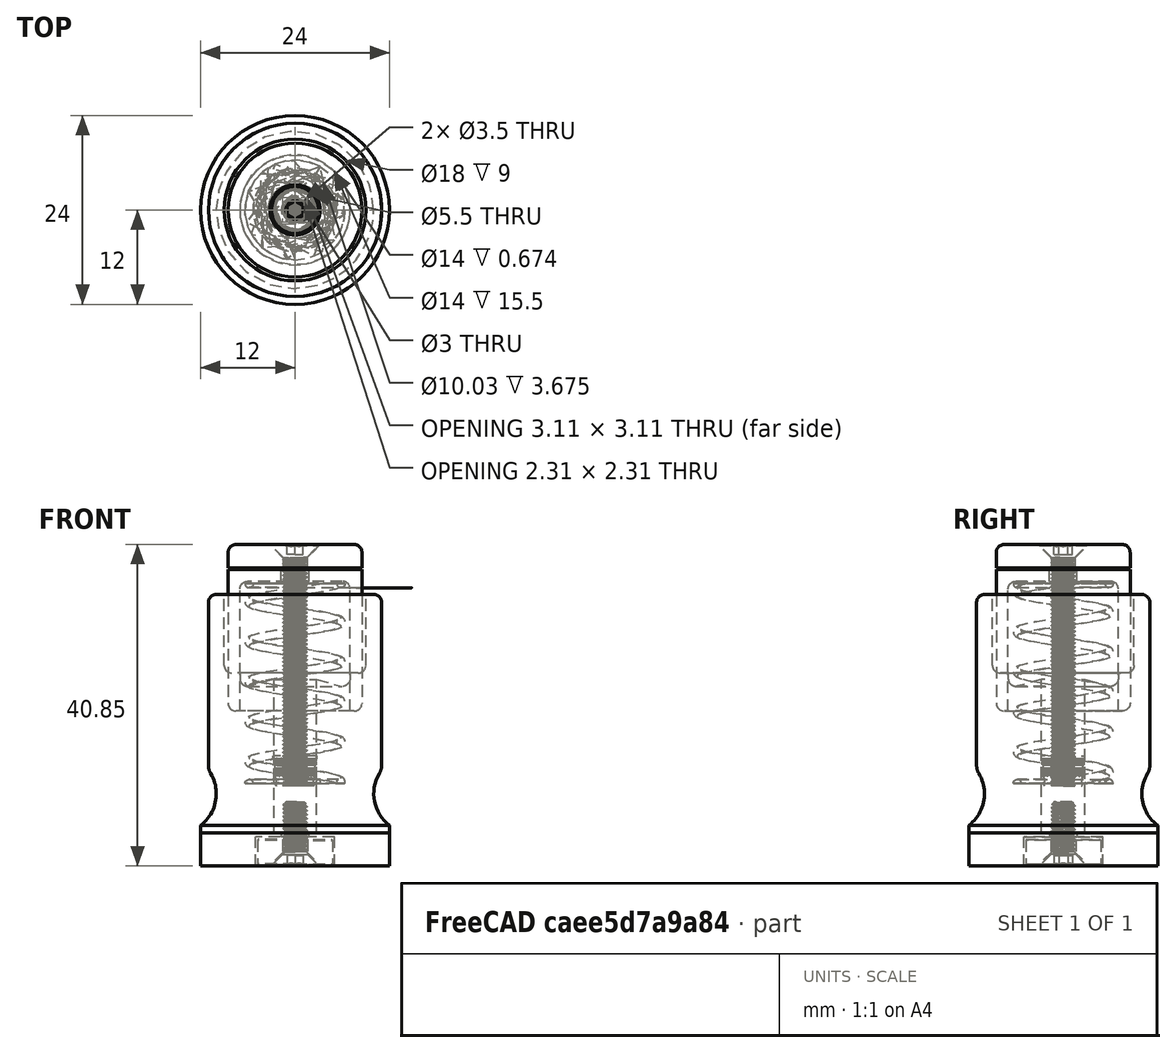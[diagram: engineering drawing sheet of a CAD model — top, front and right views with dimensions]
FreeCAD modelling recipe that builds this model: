
FCSTD DOCUMENT  (FreeCAD 1.0R39109 (Git))
Label: mag-clamp
License: All rights reserved
LicenseURL: https://en.wikipedia.org/wiki/All_rights_reserved
objects: App::FeaturePython×11, App::Link×10, Sketcher::SketchObject×9, Part::Feature×5, PartDesign::Fillet×5, PartDesign::Revolution×4, PartDesign::Body×4, PartDesign::Pocket×2, PartDesign::Groove×1, App::VarSet×1, App::Part×1, Assembly::JointGroup×1, Assembly::AssemblyObject×1, Measure::MeasureDistance×1, App::DocumentObjectGroup×1
note: 63 computed .brp shape members not serialized (recipe doc carries the construction recipe); baked Part::Feature solids carry a one-line shape summary decoded from their .brp

FEATURE [Sketcher::SketchObject] Sketch
  ArcFitTolerance = 1e-06
  AttachmentSupport = -> [XZ_Plane]
  FullyConstrained = true
  MakeInternals = false
  MapMode = 5
  Placement = pos=(0,0,0) rot=(1,0,0;1.5708rad)
  expr: Constraints[22] = VarSet.height
  sketch-geometry (14):
    g0: LineSegment StartX=0 StartY=0 StartZ=0 EndX=12 EndY=0 EndZ=0
    g1: LineSegment StartX=7 StartY=20.325 StartZ=0 EndX=7 EndY=18.325 EndZ=0
    g2: LineSegment StartX=9 StartY=30.325 StartZ=0 EndX=11 EndY=30.325 EndZ=0
    g3: LineSegment [constr] StartX=7 StartY=18.325 StartZ=0 EndX=5 EndY=18.325 EndZ=0
    g4: LineSegment [constr] StartX=5 StartY=18.325 StartZ=0 EndX=5 EndY=20.325 EndZ=0
    g5: LineSegment [constr] StartX=5 StartY=20.325 StartZ=0 EndX=0 EndY=20.325 EndZ=0
    g6: LineSegment StartX=0 StartY=0 StartZ=0 EndX=0 EndY=20.325 EndZ=0
    g7: LineSegment StartX=7 StartY=20.325 StartZ=0 EndX=9 EndY=20.325 EndZ=0
    g8: LineSegment StartX=9 StartY=20.325 StartZ=0 EndX=9 EndY=30.325 EndZ=0
    g9: LineSegment [constr] StartX=5 StartY=20.325 StartZ=0 EndX=7 EndY=20.325 EndZ=0
    g10: LineSegment StartX=11 StartY=30.325 StartZ=0 EndX=11 EndY=8 EndZ=0
    g11: LineSegment StartX=12 StartY=0 StartZ=0 EndX=12 EndY=1 EndZ=0
    g12: ArcOfCircle CenterX=15 CenterY=5 CenterZ=0 NormalX=0 NormalY=0 NormalZ=1 AngleXU=0 Radius=5 StartAngle=2.49809 EndAngle=4.06889
    g13: LineSegment StartX=0 StartY=20.325 StartZ=0 EndX=7 EndY=18.325 EndZ=0
  constraints (40):
    c: Coincident(g-1,g0)
    c: PointOnObject(g0,g-1)
    c: Vertical(g1)
    c: Horizontal(g3)
    c: Vertical(g4)
    c: Coincident(g5,g4)
    c: Horizontal(g5)
    c: Coincident(g3,g1)
    c: Horizontal(g2)
    c: Coincident(g3,g4)
    c: DistanceX(g6,g3) = 5
    c: Coincident(g6,g0)
    c: DistanceX(g0,g1) = 7
    c: DistanceX(g0,g0) = 12
    c: DistanceY(g4,g4) = 2
    c: Coincident(g6,g5)
    c: PointOnObject(g5,g-2)
    c: Horizontal(g7)
    c: Coincident(g7,g8)
    c: Vertical(g8)
    c: Coincident(g1,g7)
    c: Coincident(g2,g8)
    c: DistanceY(g0,g2) = 30.325
    c: DistanceY(g8,g8) = 10
    c: DistanceX(g7,g7) = 2
    c: DistanceX(g2,g2) = 2
    c: Coincident(g9,g4)
    c: Coincident(g9,g1)
    c: Horizontal(g9)
    c: Coincident(g10,g2)
    c: Vertical(g10)
    c: Coincident(g11,g0)
    c: Coincident(g12,g11)
    c: Coincident(g12,g10)
    c: Vertical(g11)
    c: DistanceY(g11,g11) = 1
    c: Radius(g12) = 5
    c: DistanceY(g0,g10) = 8
    c: Coincident(g13,g5)
    c: Coincident(g13,g1)
FEATURE [PartDesign::Revolution] Revolution
  Angle = 360
  Angle2 = 60
  Axis = (0,2e-16,1)
  Base = (0,0,0)
  Placement = pos=(0,0,0) rot=(1,0,0;1.5708rad)
  Profile = -> Sketch
  ReferenceAxis = -> Sketch [V_Axis]
  Refine = true
  Reversed = true
  Suppressed = false
  Type = 0
FEATURE [Part::Feature] Part__Feature  label="9657K312_Compression Spring"
  Placement = pos=(0,0,19) rot=(0,0,1;0rad)
  shape: bbox 14.01 x 14.01 x 26.49 mm, 6 faces (baked)
FEATURE [Part::Feature] Part__Feature001  label="5862K919_Neodymium Magnet"
  Placement = pos=(0,-5e-16,-2.4) rot=(1,0,0;4.71239rad)
  shape: bbox 9.525 x 9.525 x 3.175 mm, 12 faces (baked)
FEATURE [Sketcher::SketchObject] Sketch002
  ArcFitTolerance = 1e-06
  AttachmentSupport = -> [XZ_Plane001]
  FullyConstrained = true
  MakeInternals = false
  MapMode = 5
  Placement = pos=(0,0,0) rot=(1,0,0;1.5708rad)
  expr: Constraints[14] = VarSet.retainer_height
  sketch-geometry (6):
    g0: LineSegment StartX=1.75 StartY=33.5 StartZ=0 EndX=8.5 EndY=33.5 EndZ=0
    g1: LineSegment StartX=8.5 StartY=33.5 StartZ=0 EndX=8.5 EndY=15.5 EndZ=0
    g2: LineSegment StartX=8.5 StartY=15.5 StartZ=0 EndX=7 EndY=15.5 EndZ=0
    g3: LineSegment StartX=7 StartY=15.5 StartZ=0 EndX=7 EndY=32 EndZ=0
    g4: LineSegment StartX=7 StartY=32 StartZ=0 EndX=1.75 EndY=32 EndZ=0
    g5: LineSegment StartX=1.75 StartY=32 StartZ=0 EndX=1.75 EndY=33.5 EndZ=0
  constraints (18):
    c: Horizontal(g0)
    c: Coincident(g0,g1)
    c: Vertical(g1)
    c: Coincident(g1,g2)
    c: Horizontal(g2)
    c: Coincident(g2,g3)
    c: Vertical(g3)
    c: Coincident(g3,g4)
    c: Horizontal(g4)
    c: Coincident(g4,g5)
    c: Vertical(g5)
    c: Coincident(g0,g5)
    c: DistanceX(g2,g2) = 1.5
    c: DistanceY(g5,g5) = 1.5
    c: DistanceY(g1,g1) = 18
    c: DistanceX(g-1,g0) = 1.75
    c: DistanceX(g-1,g3) = 7
    c: DistanceY(g-1,g4) = 32
FEATURE [PartDesign::Revolution] Revolution001
  Angle = 360
  Angle2 = 60
  Axis = (0,2e-16,1)
  Base = (0,0,0)
  Placement = pos=(0,0,0) rot=(1,0,0;1.5708rad)
  Profile = -> Sketch002
  ReferenceAxis = -> Sketch002 [V_Axis]
  Refine = true
  Reversed = true
  Suppressed = false
  Type = 0
FEATURE [Sketcher::SketchObject] Sketch003
  ArcFitTolerance = 1e-06
  AttachmentSupport = -> [XZ_Plane002]
  FullyConstrained = false
  MakeInternals = false
  MapMode = 5
  Placement = pos=(0,0,0) rot=(1,0,0;1.5708rad)
  sketch-geometry (4):
    g0: LineSegment StartX=0 StartY=36.6662 StartZ=0 EndX=0 EndY=33.6662 EndZ=0
    g1: LineSegment StartX=0 StartY=33.6662 StartZ=0 EndX=8.5 EndY=33.6662 EndZ=0
    g2: LineSegment StartX=8.5 StartY=33.6662 StartZ=0 EndX=8.5 EndY=36.6662 EndZ=0
    g3: LineSegment StartX=8.5 StartY=36.6662 StartZ=0 EndX=0 EndY=36.6662 EndZ=0
  constraints (11):
    c: Coincident(g0,g1)
    c: Coincident(g1,g2)
    c: Coincident(g2,g3)
    c: Coincident(g3,g0)
    c: Vertical(g0)
    c: Vertical(g2)
    c: Horizontal(g1)
    c: Horizontal(g3)
    c: PointOnObject(g0,g-2)
    c: DistanceX(g3,g3) = 8.5
    c: Distance(g2,g2) = 3
FEATURE [PartDesign::Revolution] Revolution002
  Angle = 360
  Angle2 = 60
  Axis = (0,2e-16,1)
  Base = (0,0,0)
  Placement = pos=(0,0,0) rot=(1,0,0;1.5708rad)
  Profile = -> Sketch003
  ReferenceAxis = -> Sketch003 [V_Axis]
  Refine = true
  Reversed = true
  Suppressed = false
  Type = 0
FEATURE [PartDesign::Fillet] Fillet
  Base = -> Revolution002 [Edge2]
  BaseFeature = -> Revolution002
  Placement = pos=(0,0,0) rot=(1,0,0;1.5708rad)
  Radius = 1
  Refine = true
  SupportTransform = false
  Suppressed = false
  UseAllEdges = false
FEATURE [Sketcher::SketchObject] Sketch004
  ArcFitTolerance = 1e-06
  AttachmentSupport = -> [XZ_Plane002]
  ExternalGeometry = -> [Fillet]
  FullyConstrained = false
  MakeInternals = false
  MapMode = 5
  Placement = pos=(0,0,0) rot=(1,0,0;1.5708rad)
  sketch-geometry (5):
    g0: LineSegment StartX=0 StartY=36.6662 StartZ=0 EndX=0 EndY=29.3467 EndZ=0
    g1: LineSegment StartX=0 StartY=29.3467 StartZ=0 EndX=1.5 EndY=29.3467 EndZ=0
    g2: LineSegment StartX=0 StartY=36.6662 StartZ=0 EndX=3.2 EndY=36.6662 EndZ=0
    g3: LineSegment StartX=3.2 StartY=36.6662 StartZ=0 EndX=1.5 EndY=34.9662 EndZ=0
    g4: LineSegment StartX=1.5 StartY=34.9662 StartZ=0 EndX=1.5 EndY=29.3467 EndZ=0
  constraints (14):
    c: PointOnObject(g0,g-2)
    c: Vertical(g0)
    c: Coincident(g1,g0)
    c: Horizontal(g1)
    c: Coincident(g2,g0)
    c: Horizontal(g2)
    c: Coincident(g3,g2)
    c: Coincident(g4,g3)
    c: Coincident(g4,g1)
    c: Vertical(g4)
    c: DistanceX(g1,g1) = 1.5
    c: Angle(g3,g-2) = 0.785398
    c: PointOnObject(g2,g-3)
    c: DistanceY(g3,g-3) = 1.7
FEATURE [PartDesign::Groove] Groove
  Angle = 360
  Angle2 = 60
  Axis = (0,2e-16,1)
  Base = (0,0,0)
  BaseFeature = -> Fillet
  Placement = pos=(0,0,0) rot=(1,0,0;1.5708rad)
  Profile = -> Sketch004
  ReferenceAxis = -> Sketch004 [V_Axis]
  Refine = true
  Suppressed = false
  Type = 0
FEATURE [PartDesign::Body] Body002  label="Cap"
  AllowCompound = false
  Group = -> [Sketch003,Revolution002,Fillet,Sketch004,Groove]
  Origin = -> Origin002
  Tip = -> Groove
FEATURE [Sketcher::SketchObject] Sketch005
  ArcFitTolerance = 1e-06
  AttachmentSupport = -> [XZ_Plane003]
  FullyConstrained = true
  MakeInternals = false
  MapMode = 5
  Placement = pos=(0,0,0) rot=(1,0,0;1.5708rad)
  expr: Constraints[14] = VarSet.bottom_thk
  expr: Constraints[15] = VarSet.magnet_od / 2 + 0.25 mm
  sketch-geometry (6):
    g0: LineSegment StartX=0 StartY=0 StartZ=0 EndX=12 EndY=0 EndZ=0
    g1: LineSegment StartX=12 StartY=0 StartZ=0 EndX=12 EndY=-4.175 EndZ=0
    g2: LineSegment StartX=12 StartY=-4.175 StartZ=0 EndX=5.0125 EndY=-4.175 EndZ=0
    g3: LineSegment StartX=5.0125 StartY=-4.175 StartZ=0 EndX=5.0125 EndY=-0.5 EndZ=0
    g4: LineSegment StartX=5.0125 StartY=-0.5 StartZ=0 EndX=0 EndY=-0.5 EndZ=0
    g5: LineSegment StartX=0 StartY=-0.5 StartZ=0 EndX=0 EndY=0 EndZ=0
  constraints (17):
    c: Coincident(g-1,g0)
    c: PointOnObject(g0,g-1)
    c: Coincident(g0,g1)
    c: Vertical(g1)
    c: Coincident(g1,g2)
    c: Horizontal(g2)
    c: Coincident(g2,g3)
    c: Vertical(g3)
    c: Coincident(g3,g4)
    c: PointOnObject(g4,g-2)
    c: Horizontal(g4)
    c: Coincident(g4,g5)
    c: Coincident(g5,g0)
    c: DistanceX(g0,g0) = 12
    c: DistanceY(g1,g1) = 4.175
    c: DistanceX(g4,g4) = 5.0125
    c: DistanceY(g5,g5) = 0.5
FEATURE [PartDesign::Revolution] Revolution003
  Angle = 360
  Angle2 = 60
  Axis = (0,2e-16,1)
  Base = (0,0,0)
  Placement = pos=(0,0,0) rot=(1,0,0;1.5708rad)
  Profile = -> Sketch005
  ReferenceAxis = -> Sketch005 [V_Axis]
  Refine = true
  Reversed = true
  Suppressed = false
  Type = 0
FEATURE [Sketcher::SketchObject] Sketch006
  ArcFitTolerance = 1e-06
  AttachmentSupport = -> [Revolution003]
  FullyConstrained = true
  MakeInternals = false
  MapMode = 5
  Placement = pos=(0,-1e-16,-0.5) rot=(1,0,0;3.14159rad)
  sketch-geometry (1):
    g0: Circle CenterX=0 CenterY=0 CenterZ=0 NormalX=0 NormalY=0 NormalZ=1 AngleXU=0 Radius=1.75
  constraints (2):
    c: Coincident(g0,g-1)
    c: Diameter(g0) = 3.5
FEATURE [PartDesign::Pocket] Pocket001
  BaseFeature = -> Revolution003
  Direction = (0,0,1)
  Length = 5
  Length2 = 5
  Placement = pos=(0,0,0) rot=(1,0,0;1.5708rad)
  Profile = -> Sketch006
  ReferenceAxis = -> Sketch006 [N_Axis]
  Refine = true
  Suppressed = false
  Type = 1
FEATURE [PartDesign::Body] Body003  label="Magnet"
  AllowCompound = false
  Group = -> [Sketch005,Revolution003,Sketch006,Pocket001]
  Origin = -> Origin003
  Tip = -> Pocket001
FEATURE [Part::Feature] Part__Feature002  label="94180A331_Tapered Heat-Set Inserts for Plastic"
  Placement = pos=(0,0,7.9) rot=(0,0,1;0rad)
  shape: bbox 5.56 x 5.56 x 4.684 mm, 233 faces (baked)
FEATURE [Part::Feature] Part__Feature004  label="92125A128_18-8 Stainless Steel Hex Drive Flat Head Screw"
  Placement = pos=(0,0,0) rot=(0,1,0;3.14159rad)
  shape: bbox 6.001 x 6.001 x 8.204 mm, 52 faces (baked)
FEATURE [Part::Feature] Part__Feature005  label="92125A140_18-8 Stainless Steel Hex Drive Flat Head Screw"
  Placement = pos=(0,0,21.6) rot=(0,0,1;0rad)
  shape: bbox 6.001 x 6.001 x 30.2 mm, 140 faces (baked)
FEATURE [App::VarSet] VarSet
  bottom_thk = 4.175
  heatset_od = 5.5
  height = 30.325
  magnet_od = 9.525
  magnet_thk = 3.175
  retainer_height = 18
  total_height = 50
  expr: bottom_thk = magnet_thk + 1 mm
  expr: height = total_height - bottom_thk - retainer_height + 2.5 mm
FEATURE [PartDesign::Fillet] Fillet001
  Base = -> Revolution [Edge6,Edge12,Edge9]
  BaseFeature = -> Revolution
  Placement = pos=(0,0,0) rot=(1,0,0;1.5708rad)
  Radius = 1
  Refine = true
  SupportTransform = false
  Suppressed = false
  UseAllEdges = false
FEATURE [App::Link] Base  label="Base001"
  LinkedObject = -> Body
FEATURE [App::FeaturePython] GroundedJoint  # Assembly grounded joint (typed FeaturePython)
  ObjectToGround = -> Base
FEATURE [App::Link] Cap  label="Cap001"
  LinkPlacement = pos=(-3.38e-14,3.17e-14,11.7731) rot=(0,0,1;4.71239rad)
  LinkedObject = -> Body002
  Placement = pos=(-3.38e-14,3.17e-14,11.7731) rot=(0,0,1;4.71239rad)
FEATURE [App::Link] Magnet  label="Magnet001"
  LinkedObject = -> Body003
FEATURE [App::Link] _2125A140_18_8_Stainless_Steel_Hex_Drive_Flat_Head_Screw  label="92125A140_18-8 Stainless Steel Hex Drive Flat Head Screw001"
  LinkPlacement = pos=(-1.11e-14,1.43e-14,33.3243) rot=(0,0,1;0rad)
  LinkedObject = -> Part__Feature005
  Placement = pos=(-1.11e-14,1.43e-14,33.3243) rot=(0,0,1;0rad)
FEATURE [App::Link] _4180A331_Tapered_Heat_Set_Inserts_for_Plastic  label="94180A331_Tapered Heat-Set Inserts for Plastic002"
  LinkPlacement = pos=(0,0,1.9) rot=(1,0,0;3.14159rad)
  LinkedObject = -> Part__Feature002
  Placement = pos=(0,0,1.9) rot=(1,0,0;3.14159rad)
FEATURE [App::Link] _4180A331_Tapered_Heat_Set_Inserts_for_Plastic001  label="94180A331_Tapered Heat-Set Inserts for Plastic003"
  LinkPlacement = pos=(0,4.5e-15,17.6393) rot=(0,0,1;4.71239rad)
  LinkedObject = -> Part__Feature002
  Placement = pos=(0,4.5e-15,17.6393) rot=(0,0,1;4.71239rad)
FEATURE [App::Link] _2125A128_18_8_Stainless_Steel_Hex_Drive_Flat_Head_Screw  label="92125A128_18-8 Stainless Steel Hex Drive Flat Head Screw001"
  LinkPlacement = pos=(-5.3e-15,3.2e-15,0.0975) rot=(1,0,0;3.14159rad)
  LinkedObject = -> Part__Feature004
  Placement = pos=(-5.3e-15,3.2e-15,0.0975) rot=(1,0,0;3.14159rad)
FEATURE [App::Link] _862K919_Neodymium_Magnet  label="5862K919_Neodymium Magnet001"
  LinkPlacement = pos=(-5.6e-15,3.5e-15,-2.0875) rot=(-0.57735,0.57735,-0.57735;2.0944rad)
  LinkedObject = -> Part__Feature001
  Placement = pos=(-5.6e-15,3.5e-15,-2.0875) rot=(-0.57735,0.57735,-0.57735;2.0944rad)
FEATURE [Sketcher::SketchObject] Sketch008
  ArcFitTolerance = 1e-06
  AttachmentSupport = -> [Part__Feature]
  FullyConstrained = false
  MakeInternals = false
  MapMode = 5
  Placement = pos=(0,0,6.3) rot=(1,0,0;3.14159rad)
  sketch-geometry (1):
    g0: Circle CenterX=0 CenterY=0 CenterZ=0 NormalX=0 NormalY=0 NormalZ=1 AngleXU=0 Radius=4.4961
  constraints (1):
    c: Coincident(g0,g-1)
FEATURE [App::Link] Spring  label="Spring001"
  LinkPlacement = pos=(0,4.5e-15,12.2393) rot=(0,0,1;4.71239rad)
  LinkedObject = -> Part
  Placement = pos=(0,4.5e-15,12.2393) rot=(0,0,1;4.71239rad)
FEATURE [Sketcher::SketchObject] Sketch010
  ArcFitTolerance = 1e-06
  AttachmentSupport = -> [Fillet001]
  FullyConstrained = true
  MakeInternals = false
  MapMode = 5
  Placement = pos=(0,6.7e-15,30.325) rot=(0,0,1;3.14159rad)
  expr: Constraints[1] = VarSet.heatset_od
  sketch-geometry (1):
    g0: Circle CenterX=0 CenterY=0 CenterZ=0 NormalX=0 NormalY=0 NormalZ=1 AngleXU=0 Radius=2.75
  constraints (2):
    c: Coincident(g0,g-1)
    c: Diameter(g0) = 5.5
FEATURE [PartDesign::Pocket] Pocket
  BaseFeature = -> Fillet001
  Direction = (0,0,-1)
  Length = 5
  Length2 = 5
  Placement = pos=(0,0,0) rot=(1,0,0;1.5708rad)
  Profile = -> Sketch010
  ReferenceAxis = -> Sketch010 [N_Axis]
  Refine = true
  Suppressed = false
  Type = 1
FEATURE [PartDesign::Fillet] Fillet002
  Base = -> Pocket [Edge3]
  BaseFeature = -> Pocket
  Placement = pos=(0,0,0) rot=(1,0,0;1.5708rad)
  Radius = 2
  Refine = true
  SupportTransform = false
  Suppressed = false
  UseAllEdges = false
FEATURE [PartDesign::Body] Body  label="Base"
  AllowCompound = false
  Group = -> [Sketch,Revolution,Fillet001,Sketch010,Pocket,Fillet002]
  Origin = -> Origin
  Tip = -> Fillet002
FEATURE [PartDesign::Fillet] Fillet003
  Base = -> Revolution001 [Edge3]
  BaseFeature = -> Revolution001
  Placement = pos=(0,0,0) rot=(1,0,0;1.5708rad)
  Radius = 1
  Refine = true
  SupportTransform = false
  Suppressed = false
  UseAllEdges = false
FEATURE [App::FeaturePython] Joint008  label="Fixed006"  # Assembly joint (typed FeaturePython)
  Activated = true
  AngleMax = 0
  AngleMin = 0
  Detach1 = false
  Detach2 = false
  Distance = 0
  Distance2 = 0
  EnableAngleMax = false
  EnableAngleMin = false
  EnableLengthMax = false
  EnableLengthMin = false
  JointType = 0 (Fixed)
  LengthMax = 0
  LengthMin = 0
  Placement1 = pos=(0,0,1.9) rot=(0,0,1;0rad)
  Reference1 = -> Assembly [_4180A331_Tapered_Heat_Set_Inserts_for_Plastic.Edge61,_4180A331_Tapered_Heat_Set_Inserts_for_Plastic.Edge61]
  Reference2 = -> Assembly [Base.?Edge13,Base.?Edge13]
FEATURE [App::FeaturePython] Joint  label="Fixed"  # Assembly joint (typed FeaturePython)
  Activated = true
  AngleMax = 0
  AngleMin = 0
  Detach1 = false
  Detach2 = false
  Distance = 0
  Distance2 = 0
  EnableAngleMax = false
  EnableAngleMin = false
  EnableLengthMax = false
  EnableLengthMin = false
  JointType = 0 (Fixed)
  LengthMax = 0
  LengthMin = 0
  Placement1 = pos=(0,0,0) rot=(1,0,0;3.14159rad)
  Reference1 = -> Assembly [Magnet.Edge1,Magnet.Edge1]
  Reference2 = -> Assembly [Base.?Edge16,Base.?Edge16]
FEATURE [App::FeaturePython] Joint005  label="Fixed003"  # Assembly joint (typed FeaturePython)
  Activated = true
  AngleMax = 0
  AngleMin = 0
  Detach1 = false
  Detach2 = false
  Distance = 0
  Distance2 = 0
  EnableAngleMax = false
  EnableAngleMin = false
  EnableLengthMax = false
  EnableLengthMin = false
  JointType = 0 (Fixed)
  LengthMax = 0
  LengthMin = 0
  Placement1 = pos=(3.5e-15,-1.5875,5.2e-15) rot=(0.57735,-0.57735,0.57735;2.0944rad)
  Placement2 = pos=(0,-1e-16,-0.5) rot=(1,0,0;3.14159rad)
  Reference1 = -> Assembly [_862K919_Neodymium_Magnet.Edge24,_862K919_Neodymium_Magnet.Edge24]
  Reference2 = -> Assembly [Magnet.Edge8,Magnet.Edge8]
FEATURE [App::FeaturePython] Joint006  label="Fixed004"  # Assembly joint (typed FeaturePython)
  Activated = true
  AngleMax = 0
  AngleMin = 0
  Detach1 = false
  Detach2 = false
  Distance = 0
  Distance2 = 0
  EnableAngleMax = false
  EnableAngleMin = false
  EnableLengthMax = false
  EnableLengthMin = false
  JointType = 0 (Fixed)
  LengthMax = 0
  LengthMin = 0
  Placement1 = pos=(0,-1e-16,0.915) rot=(0,0,-1;1.5708rad)
  Placement2 = pos=(0,-1.27,0) rot=(0,0.707107,0.707107;3.14159rad)
  Reference1 = -> Assembly [_2125A128_18_8_Stainless_Steel_Hex_Drive_Flat_Head_Screw.Face29,_2125A128_18_8_Stainless_Steel_Hex_Drive_Flat_Head_Screw.Face29]
  Reference2 = -> Assembly [_862K919_Neodymium_Magnet.Face3,_862K919_Neodymium_Magnet.Face3]
FEATURE [App::FeaturePython] Joint004  label="Fixed002"  # Assembly joint (typed FeaturePython)
  Activated = true
  AngleMax = 0
  AngleMin = 0
  Detach1 = false
  Detach2 = false
  Distance = 0
  Distance2 = 0
  EnableAngleMax = false
  EnableAngleMin = false
  EnableLengthMax = false
  EnableLengthMin = false
  JointType = 0 (Fixed)
  LengthMax = 0
  LengthMin = 0
  Placement1 = pos=(0,7.4e-15,33.4662) rot=(0,0,1;0rad)
  Placement2 = pos=(0,-1e-16,11.915) rot=(0,0,-1;1.5708rad)
  Reference1 = -> Assembly [Cap.Face6,Cap.Face6]
  Reference2 = -> Assembly [_2125A140_18_8_Stainless_Steel_Hex_Drive_Flat_Head_Screw.Face119,_2125A140_18_8_Stainless_Steel_Hex_Drive_Flat_Head_Screw.Face119]
FEATURE [App::FeaturePython] Joint010  label="Fixed008"  # Assembly joint (typed FeaturePython)
  Activated = true
  AngleMax = 0
  AngleMin = 0
  Detach1 = false
  Detach2 = false
  Distance = 0
  Distance2 = 0
  EnableAngleMax = false
  EnableAngleMin = false
  EnableLengthMax = false
  EnableLengthMin = false
  JointType = 0 (Fixed)
  LengthMax = 0
  LengthMin = 0
  Offset2 = pos=(0,0,-1) rot=(0,0,1;0rad)
  Placement2 = pos=(0,4.5e-15,18.5393) rot=(0,0,-1;1.5708rad)
  Reference1 = -> Assembly [Spring.Sketch008.Edge1,Spring.Sketch008.Edge1]
  Reference2 = -> Assembly [Base.Edge19,Base.Edge19]
FEATURE [App::FeaturePython] Joint002  label="Cylindrical"  # Assembly joint (typed FeaturePython)
  Activated = true
  AngleMax = 0
  AngleMin = 0
  Detach1 = false
  Detach2 = false
  Distance = 0
  Distance2 = 0
  EnableAngleMax = false
  EnableAngleMin = false
  EnableLengthMax = false
  EnableLengthMin = false
  JointType = 2 (Cylindrical)
  LengthMax = 0
  LengthMin = 0
  Placement1 = pos=(6.1e-14,6.27e-14,-36.9393) rot=(0,0,-1;4.71239rad)
  Reference1 = -> Assembly [Retainer.?Face2,Retainer.?Face2]
  Reference2 = -> Assembly [Base.?Face6,Base.Edge25]
FEATURE [App::FeaturePython] Joint003  label="Fixed001"  # Assembly joint (typed FeaturePython)
  Activated = true
  AngleMax = 0
  AngleMin = 0
  Detach1 = false
  Detach2 = false
  Distance = 0
  Distance2 = 0
  EnableAngleMax = false
  EnableAngleMin = false
  EnableLengthMax = false
  EnableLengthMin = false
  JointType = 0 (Fixed)
  LengthMax = 0
  LengthMin = 0
  Placement1 = pos=(0,7.5e-15,33.6662) rot=(1,0,0;3.14159rad)
  Placement2 = pos=(0,7.4e-15,33.5) rot=(1,0,0;3.14159rad)
  Reference1 = -> Assembly [Cap.Edge3,Cap.Edge3]
  Reference2 = -> Assembly [Retainer.Edge13,Retainer.Edge13]
FEATURE [Sketcher::SketchObject] Sketch009
  ArcFitTolerance = 1e-06
  AttachmentSupport = -> [Part__Feature]
  FullyConstrained = false
  MakeInternals = false
  MapMode = 5
  Placement = pos=(0,0,31.7) rot=(0,0,1;0rad)
  sketch-geometry (1):
    g0: Circle CenterX=0 CenterY=0 CenterZ=0 NormalX=0 NormalY=0 NormalZ=1 AngleXU=0 Radius=3.7823
  constraints (1):
    c: Coincident(g0,g-1)
FEATURE [App::Part] Part  label="Spring"
  Group = -> [Part__Feature,Sketch008,Sketch009]
  Origin = -> Origin005
FEATURE [App::Link] Retainer  label="Retainer001"
  LinkPlacement = pos=(-3.35e-14,3.16e-14,11.9393) rot=(0,0,1;4.71239rad)
  LinkedObject = -> Body001
  Placement = pos=(-3.35e-14,3.16e-14,11.9393) rot=(0,0,1;4.71239rad)
FEATURE [PartDesign::Fillet] Fillet004
  Base = -> Fillet003 [Edge10]
  BaseFeature = -> Fillet003
  Placement = pos=(0,0,0) rot=(1,0,0;1.5708rad)
  Radius = 1
  Refine = true
  SupportTransform = false
  Suppressed = false
  UseAllEdges = false
FEATURE [PartDesign::Body] Body001  label="Retainer"
  AllowCompound = false
  Group = -> [Sketch002,Revolution001,Fillet003,Fillet004]
  Origin = -> Origin001
  Tip = -> Fillet004
FEATURE [App::FeaturePython] Joint011  label="Fixed009"  # Assembly joint (typed FeaturePython)
  Activated = true
  AngleMax = 0
  AngleMin = 0
  Detach1 = false
  Detach2 = false
  Distance = 0
  Distance2 = 0
  EnableAngleMax = false
  EnableAngleMin = false
  EnableLengthMax = false
  EnableLengthMin = false
  JointType = 0 (Fixed)
  LengthMax = 0
  LengthMin = 0
  Placement1 = pos=(0,0,1.9) rot=(0,0,1;0rad)
  Placement2 = pos=(0,4.5e-15,19.5393) rot=(0,0,-1;1.5708rad)
  Reference1 = -> Assembly [_4180A331_Tapered_Heat_Set_Inserts_for_Plastic001.Edge61,_4180A331_Tapered_Heat_Set_Inserts_for_Plastic001.Edge61]
  Reference2 = -> Assembly [Base.Edge19,Base.Edge19]
FEATURE [App::FeaturePython] Joint012  label="Fixed010"  # Assembly joint (typed FeaturePython)
  Activated = true
  AngleMax = 0
  AngleMin = 0
  Detach1 = false
  Detach2 = false
  Distance = 0
  Distance2 = 0
  EnableAngleMax = false
  EnableAngleMin = false
  EnableLengthMax = false
  EnableLengthMin = false
  JointType = 0 (Fixed)
  LengthMax = 0
  LengthMin = 0
  Placement1 = pos=(0,7.1e-15,32) rot=(1,0,0;3.14159rad)
  Reference1 = -> Assembly [Retainer.Edge5,Retainer.Edge5]
  Reference2 = -> Assembly [Spring.Sketch009.Edge1,Spring.Sketch009.Edge1]
FEATURE [Assembly::JointGroup] Joints
  Group = -> [GroundedJoint,Joint,Joint002,Joint003,Joint004,Joint005,Joint006,Joint008,Joint010,Joint011,Joint012]
FEATURE [Assembly::AssemblyObject] Assembly
  Group = -> [Joints,Base,GroundedJoint,Retainer,Cap,Magnet,_2125A140_18_8_Stainless_Steel_Hex_Drive_Flat_Head_Screw,_4180A331_Tapered_Heat_Set_Inserts_for_Plastic,_4180A331_Tapered_Heat_Set_Inserts_for_Plastic001,_2125A128_18_8_Stainless_Steel_Hex_Drive_Flat_Head_Screw,Joint,Joint002,Joint003,Joint004,_862K919_Neodymium_Magnet,Joint005,Joint006,Joint008,Spring,Joint010,Joint011,Joint012]
  Origin = -> Origin004
  Type = Assembly
FEATURE [Measure::MeasureDistance] Distance  label="Distance: 49.61 mm"
  Distance = 49.6143
  DistanceX = 3.6e-15
  DistanceY = 2.8e-15
  DistanceZ = 49.6143
  Element1 = -> Assembly [Magnet.Pocket001.Edge3]
  Element2 = -> Assembly [Cap.Groove.Edge3]
  Position1 = (0,-9e-16,-4.175)
  Position2 = (3.6e-15,1.8e-15,45.4393)
FEATURE [App::DocumentObjectGroup] Measurements
  Group = -> [Distance]
